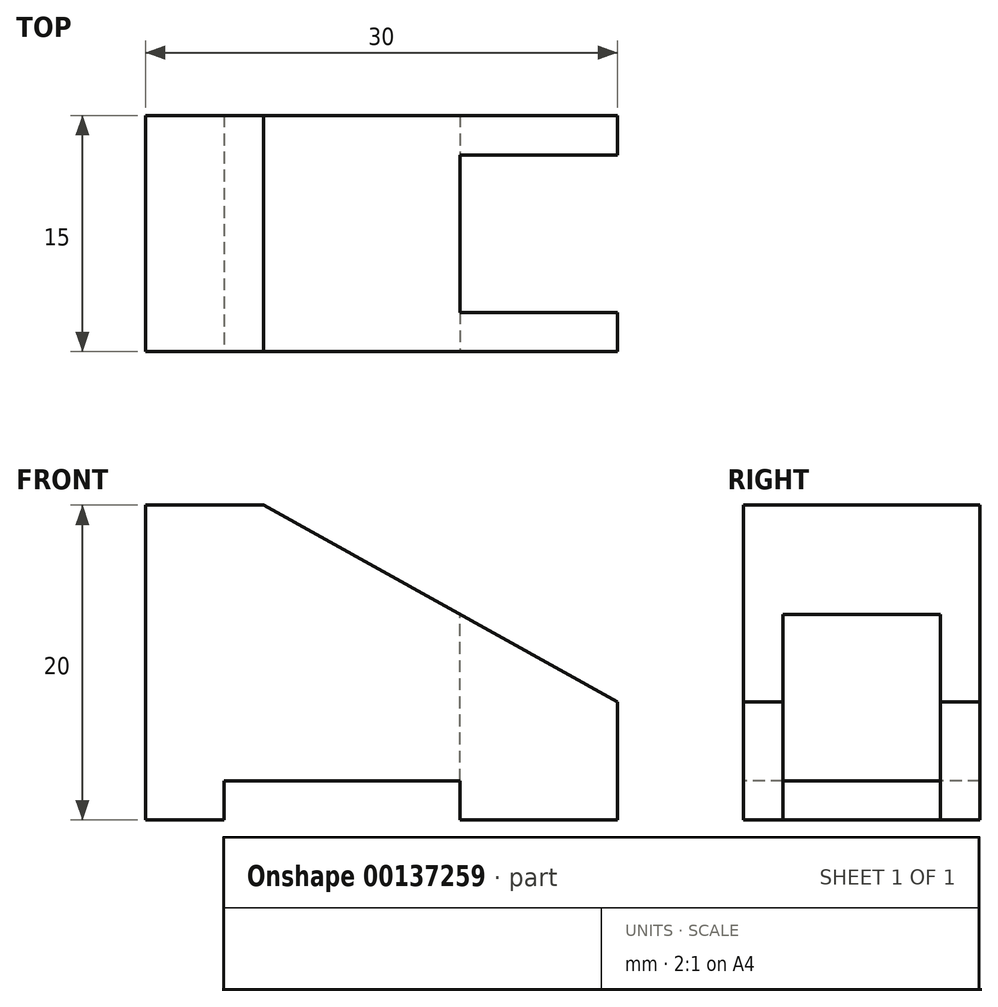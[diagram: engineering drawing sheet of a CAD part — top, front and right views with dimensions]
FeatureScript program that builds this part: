
annotation { "Feature Type Name" : "Feature", "Feature Type Description" : "" }
export const myFeature = defineFeature(function(context is Context, id is Id, definition is map)
    precondition{}
    {
        {
            var Q0;
            Q0=qCreatedBy(makeId("Front.planeOp"),FACE);
            var sketch = newSketch(context, id + "F0", { "sketchPlane" : qUnion([Q0])});
            skLineSegment(sketch, "E0", {"start": v(0, 0) * mm, "end": v(0, 20) * mm});
            skLineSegment(sketch, "E1", {"start": v(0, 20) * mm, "end": v(7.5, 20) * mm});
            skLineSegment(sketch, "E2", {"start": v(7.5, 20) * mm, "end": v(30, 7.5) * mm});
            skLineSegment(sketch, "E3", {"start": v(30, 7.5) * mm, "end": v(30, 0) * mm});
            skLineSegment(sketch, "E4", {"start": v(30, 0) * mm, "end": v(0, 0) * mm});
            skLineSegment(sketch, "E5", {"start": v(20, 0) * mm, "end": v(20, 13.06) * mm});
            skLineSegment(sketch, "E6", {"start": v(20, 13.06) * mm, "end": v(30, 7.5) * mm});
            skLineSegment(sketch, "E7", {"start": v(30, 0) * mm, "end": v(20, 0) * mm});
            skSolve(sketch);
        }
        {
            var Q0;
            Q0 = qSketchRegion(id + "F0", true);
            extrude(context, id + "F1", {"entities" : qUnion([Q0]), "endBound" : BoundingType.SYMMETRIC, "oppositeDirection" : true, "depth" : 15 * mm, "hasSecondDirection" : true, "secondDirectionOppositeDirection" : true, "secondDirectionDepth" : 25 * mm});
        }
        {
            var Q0;
            Q0=makeQuery(id+"F1.opExtrude","CAP_FACE",FACE,{"disambiguationData":[OSD([sQuery(id+"F0.wireOp",EDGE,"E0"),sQuery(id+"F0.wireOp",EDGE,"E1"),sQuery(id+"F0.wireOp",EDGE,"E2"),sQuery(id+"F0.wireOp",EDGE,"E3"),sQuery(id+"F0.wireOp",EDGE,"E4"),sQuery(id+"F0.wireOp",EDGE,"E6"),sQuery(id+"F0.wireOp",EDGE,"E7")])],"isStart":true});
            var sketch = newSketch(context, id + "F2", { "sketchPlane" : qUnion([Q0])});
            skLineSegment(sketch, "E8.bottom", {"start": v(5, 0) * mm, "end": v(20, 0) * mm});
            skLineSegment(sketch, "E8.top", {"start": v(5, 2.5) * mm, "end": v(20, 2.5) * mm});
            skLineSegment(sketch, "E8.left", {"start": v(5, 0) * mm, "end": v(5, 2.5) * mm});
            skLineSegment(sketch, "E8.right", {"start": v(20, 0) * mm, "end": v(20, 2.5) * mm});
            skSolve(sketch);
        }
        {
            var Q0;
            Q0=makeQuery(id+"F2.imprint","IMPRINT",FACE,{"disambiguationData":[TD([[makeQuery(id+"F2.imprint","IMPRINT",EDGE,{"derivedFrom":sQuery(id+"F2.wireOp",EDGE,"E8.bottom")}),-1.0]])]});
            extrude(context, id + "F3", {"entities" : qUnion([Q0]), "operationType" : NewBodyOperationType.REMOVE, "endBound" : BoundingType.THROUGH_ALL, "oppositeDirection" : true, "depth" : 25 * mm});
        }
        {
            var Q0;
            Q0=makeQuery(id+"F0.imprint","IMPRINT",FACE,{"disambiguationData":[TD([[makeQuery(id+"F0.imprint","IMPRINT",EDGE,{"derivedFrom":sQuery(id+"F0.wireOp",EDGE,"E3")}),-1.0]])]});
            extrude(context, id + "F4", {"entities" : qUnion([Q0]), "operationType" : NewBodyOperationType.REMOVE, "endBound" : BoundingType.SYMMETRIC, "depth" : 10 * mm});
        }
    });
